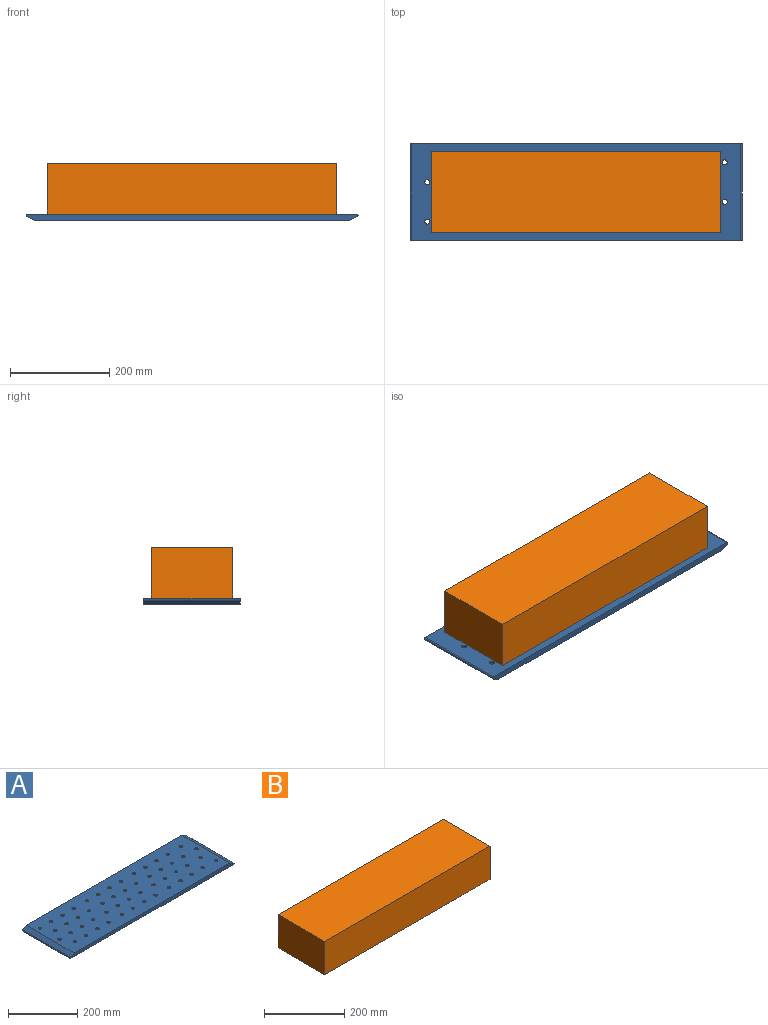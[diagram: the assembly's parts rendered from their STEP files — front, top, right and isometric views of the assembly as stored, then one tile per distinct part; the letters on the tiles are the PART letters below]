
ASSEMBLY  parts=2 mates=1
PART A: 60 faces, bbox 670.2x195.7x12.7 mm
  f0: plane 670.16x12.7mm, normal (0,1,0), area 8359.9mm2, adj f1,f55,f56,f57,f58,f59
  f1: plane 665.08x195.71mm, normal (0,0,-1), area 125816.4mm2, adj f0,f2,f3,f4,f5,f6,f7,f8
  f2: cylinder r=5.16mm len=12.7mm, axis (0,0,-1), area 411.6mm2, adj f1,f57
  f3: cylinder r=5.16mm len=12.7mm, axis (0,0,-1), area 411.6mm2, adj f1,f57
  f4: cylinder r=5.16mm len=12.7mm, axis (0,0,-1), area 411.6mm2, adj f1,f57
  f5: cylinder r=5.16mm len=12.7mm, axis (0,0,-1), area 411.6mm2, adj f1,f57
  f6: cylinder r=5.16mm len=12.7mm, axis (0,0,-1), area 411.6mm2, adj f1,f57
  f7: cylinder r=5.16mm len=12.7mm, axis (0,0,-1), area 411.6mm2, adj f1,f57
  f8: cylinder r=5.16mm len=12.7mm, axis (0,0,-1), area 411.6mm2, adj f1,f57
  f9: cylinder r=5.16mm len=12.7mm, axis (0,0,-1), area 411.6mm2, adj f1,f57
  f10: cylinder r=5.16mm len=12.7mm, axis (0,0,-1), area 411.6mm2, adj f1,f57
  f11: cylinder r=5.16mm len=12.7mm, axis (0,0,-1), area 411.6mm2, adj f1,f57
  f12: cylinder r=5.16mm len=12.7mm, axis (0,0,-1), area 411.6mm2, adj f1,f57
  f13: cylinder r=5.16mm len=12.7mm, axis (0,0,-1), area 411.6mm2, adj f1,f57
  f14: cylinder r=5.16mm len=12.7mm, axis (0,0,-1), area 411.6mm2, adj f1,f57
  f15: cylinder r=5.16mm len=12.7mm, axis (0,0,-1), area 411.6mm2, adj f1,f57
  f16: cylinder r=5.16mm len=12.7mm, axis (0,0,-1), area 411.6mm2, adj f1,f57
  f17: cylinder r=5.16mm len=12.7mm, axis (0,0,-1), area 411.6mm2, adj f1,f57
  f18: cylinder r=5.16mm len=12.7mm, axis (0,0,-1), area 411.6mm2, adj f1,f57
  f19: cylinder r=5.16mm len=12.7mm, axis (0,0,-1), area 411.6mm2, adj f1,f57
  f20: cylinder r=5.16mm len=12.7mm, axis (0,0,-1), area 411.6mm2, adj f1,f57
  f21: cylinder r=5.16mm len=12.7mm, axis (0,0,-1), area 411.6mm2, adj f1,f57
  f22: cylinder r=5.16mm len=12.7mm, axis (0,0,-1), area 411.6mm2, adj f1,f57
  f23: cylinder r=5.16mm len=12.7mm, axis (0,0,-1), area 411.6mm2, adj f1,f57
  f24: cylinder r=5.16mm len=12.7mm, axis (0,0,-1), area 411.6mm2, adj f1,f57
  f25: cylinder r=5.16mm len=12.7mm, axis (0,0,-1), area 411.6mm2, adj f1,f57
  f26: cylinder r=5.16mm len=12.7mm, axis (0,0,-1), area 411.6mm2, adj f1,f57
  f27: cylinder r=5.16mm len=12.7mm, axis (0,0,-1), area 411.6mm2, adj f1,f57
  f28: cylinder r=5.16mm len=12.7mm, axis (0,0,-1), area 411.6mm2, adj f1,f57
  f29: cylinder r=5.16mm len=12.7mm, axis (0,0,-1), area 411.6mm2, adj f1,f57
  f30: cylinder r=5.16mm len=12.7mm, axis (0,0,-1), area 411.6mm2, adj f1,f57
  f31: cylinder r=5.16mm len=12.7mm, axis (0,0,-1), area 411.6mm2, adj f1,f57
  f32: cylinder r=5.16mm len=12.7mm, axis (0,0,-1), area 411.6mm2, adj f1,f57
  f33: cylinder r=5.16mm len=12.7mm, axis (0,0,-1), area 411.6mm2, adj f1,f57
  f34: cylinder r=5.16mm len=12.7mm, axis (0,0,-1), area 411.6mm2, adj f1,f57
  f35: cylinder r=5.16mm len=12.7mm, axis (0,0,-1), area 411.6mm2, adj f1,f57
  f36: cylinder r=5.16mm len=12.7mm, axis (0,0,-1), area 411.6mm2, adj f1,f57
  f37: cylinder r=5.16mm len=12.7mm, axis (0,0,-1), area 411.6mm2, adj f1,f57
  f38: cylinder r=5.16mm len=12.7mm, axis (0,0,-1), area 411.6mm2, adj f1,f57
  f39: cylinder r=5.16mm len=12.7mm, axis (0,0,-1), area 411.6mm2, adj f1,f57
  f40: cylinder r=5.16mm len=12.7mm, axis (0,0,-1), area 411.6mm2, adj f1,f57
  f41: cylinder r=5.16mm len=12.7mm, axis (0,0,-1), area 411.6mm2, adj f1,f57
  f42: cylinder r=5.16mm len=12.7mm, axis (0,0,-1), area 411.6mm2, adj f1,f57
  f43: cylinder r=5.16mm len=12.7mm, axis (0,0,-1), area 411.6mm2, adj f1,f57
  f44: cylinder r=5.16mm len=12.7mm, axis (0,0,-1), area 411.6mm2, adj f1,f57
  f45: cylinder r=5.16mm len=12.7mm, axis (0,0,-1), area 411.6mm2, adj f1,f57
  f46: cylinder r=5.16mm len=12.7mm, axis (0,0,-1), area 411.6mm2, adj f1,f57
  f47: cylinder r=5.16mm len=12.7mm, axis (0,0,-1), area 411.6mm2, adj f1,f57
  f48: cylinder r=5.16mm len=12.7mm, axis (0,0,-1), area 411.6mm2, adj f1,f57
  f49: cylinder r=5.16mm len=12.7mm, axis (0,0,-1), area 411.6mm2, adj f1,f57
  f50: cylinder r=5.16mm len=12.7mm, axis (0,0,-1), area 411.6mm2, adj f1,f57
  f51: cylinder r=5.16mm len=12.7mm, axis (0,0,-1), area 411.6mm2, adj f1,f57
  f52: cylinder r=5.16mm len=12.7mm, axis (0,0,-1), area 411.6mm2, adj f1,f57
  f53: cylinder r=5.16mm len=12.7mm, axis (0,0,-1), area 411.6mm2, adj f1,f57
  f54: plane 670.16x12.7mm, normal (0,-1,0), area 8359.9mm2, adj f1,f55,f56,f57,f58,f59
  f55: plane 195.71x15.78mm, normal (0.45,0,0.89), area 3452mm2, adj f0,f54,f57,f59
  f56: plane 195.71x15.78mm, normal (-0.45,0,0.89), area 3452mm2, adj f0,f54,f57,f58
  f57: plane 635.8x195.71mm, normal (0,0,1), area 120085.8mm2, adj f0,f2,f3,f4,f5,f6,f7,f8
  f58: cylinder r=2.54mm len=195.71mm, axis (0,1,0), area 1331.2mm2, adj f0,f1,f54,f56
  f59: cylinder r=2.54mm len=195.71mm, axis (0,1,0), area 1331.2mm2, adj f0,f1,f54,f55
PART B: 6 faces, bbox 584.2x165.1x101.6 mm
  f0: plane 165.1x101.6mm, normal (1,0,0), area 16774.2mm2, adj f1,f3,f4,f5
  f1: plane 584.2x101.6mm, normal (0,1,0), area 59354.7mm2, adj f0,f2,f4,f5
  f2: plane 165.1x101.6mm, normal (-1,0,0), area 16774.2mm2, adj f1,f3,f4,f5
  f3: plane 584.2x101.6mm, normal (0,-1,0), area 59354.7mm2, adj f0,f2,f4,f5
  f4: plane 584.2x165.1mm, normal (0,0,1), area 96451.4mm2, adj f0,f1,f2,f3
  f5: plane 584.2x165.1mm, normal (0,0,-1), area 96451.4mm2, adj f0,f1,f2,f3
PLACE A rot(axis=(1,0,0),180deg) t=(38.87,-260.68,116.87)mm
PLACE B rot(axis=(0,1,0),180deg) t=(8.65,-200.92,171.23)mm
MATE fastened B.f4 <-> A.f1  axis (0,0,-1) through (8.65,-200.92,69.63)mm
